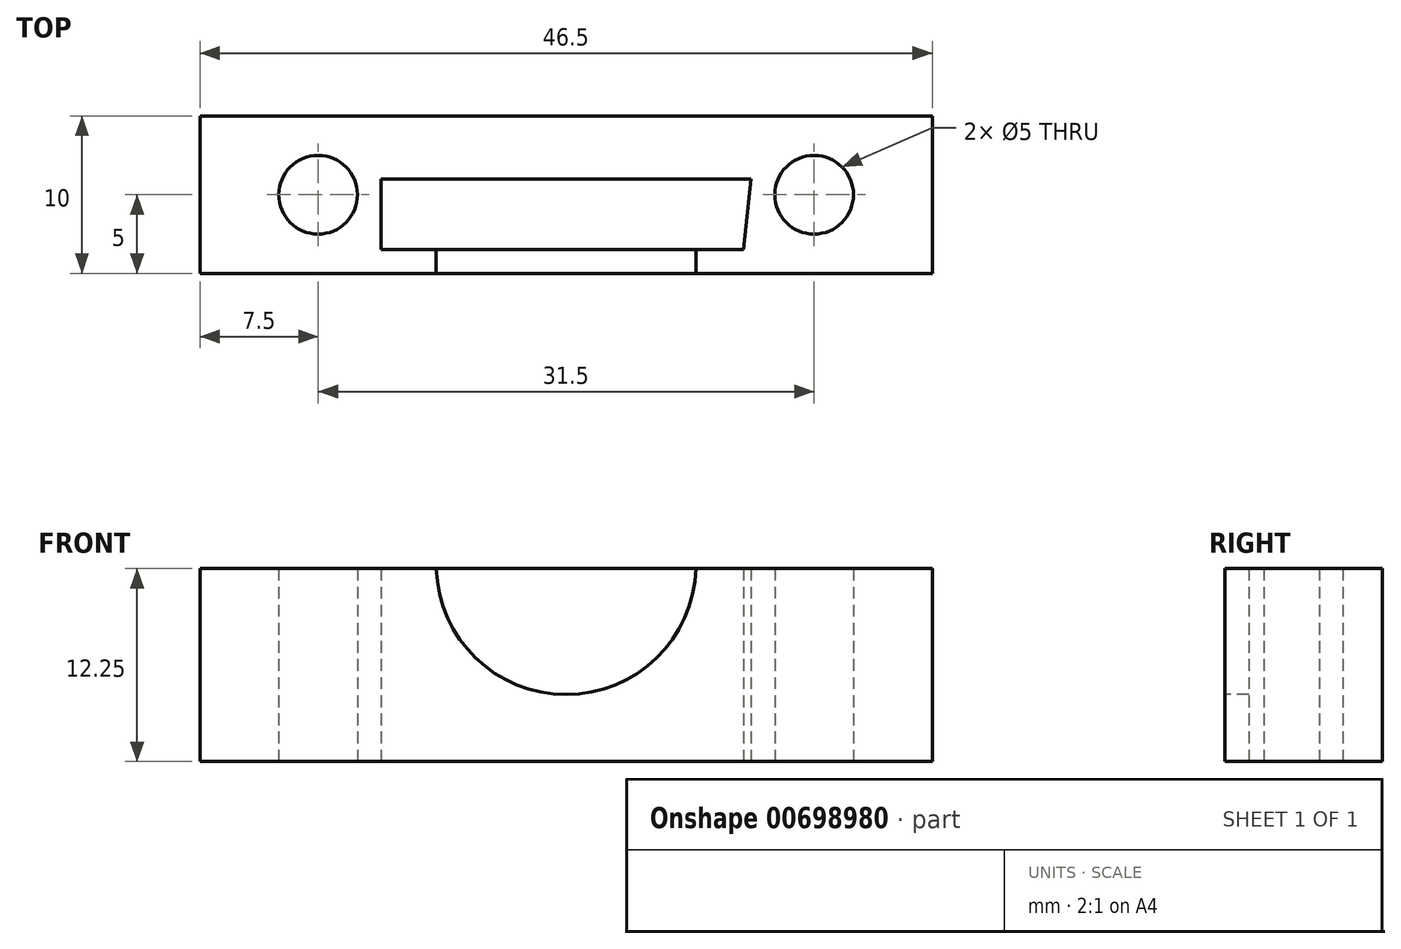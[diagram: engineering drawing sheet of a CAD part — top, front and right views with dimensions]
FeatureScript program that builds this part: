
annotation { "Feature Type Name" : "Feature", "Feature Type Description" : "" }
export const myFeature = defineFeature(function(context is Context, id is Id, definition is map)
    precondition{}
    {
        {
            var Q0;
            Q0=qCreatedBy(makeId("Top.planeOp"),FACE);
            var sketch = newSketch(context, id + "F0", { "sketchPlane" : qUnion([Q0])});
            skCircle(sketch, "E0", {"center": v(-15.75, 0) * mm, "radius": 2.5 * mm});
            skCircle(sketch, "E1", {"center": v(15.75, 0) * mm, "radius": 2.5 * mm});
            skLineSegment(sketch, "E2.bottom", {"start": v(-23.25, 5) * mm, "end": v(23.25, 5) * mm});
            skLineSegment(sketch, "E2.top", {"start": v(-23.25, -5) * mm, "end": v(23.25, -5) * mm});
            skLineSegment(sketch, "E2.left", {"start": v(-23.25, 5) * mm, "end": v(-23.25, -5) * mm});
            skLineSegment(sketch, "E2.right", {"start": v(23.25, 5) * mm, "end": v(23.25, -5) * mm});
            skLineSegment(sketch, "E3", {"start": v(-11.75, -3.47) * mm, "end": v(11.25, -3.47) * mm});
            skLineSegment(sketch, "E4.top", {"start": v(-11.75, 1) * mm, "end": v(11.75, 1) * mm});
            skLineSegment(sketch, "E5", {"start": v(-11.75, 1) * mm, "end": v(-11.75, -3.47) * mm});
            skLineSegment(sketch, "E6", {"start": v(11.75, 1) * mm, "end": v(11.25, -3.47) * mm});
            skSolve(sketch);
        }
        {
            var Q0;
            Q0=makeQuery(id+"F0.imprint","IMPRINT",FACE,{"disambiguationData":[TD([[makeQuery(id+"F0.imprint","IMPRINT",EDGE,{"derivedFrom":sQuery(id+"F0.wireOp",EDGE,"E0")}),-1.0]])]});
            extrude(context, id + "F1", {"entities" : qUnion([Q0]), "depth" : 12.25 * mm, "offsetDistance" : 25 * mm});
        }
        {
            var Q0;
            Q0=makeQuery(id+"F1.opExtrude","SWEPT_FACE",FACE,{"disambiguationData":[OSD([sQuery(id+"F0.wireOp",EDGE,"E2.top")])]});
            var sketch = newSketch(context, id + "F2", { "sketchPlane" : qUnion([Q0])});
            skCircle(sketch, "E7", {"center": v(0, 12.5) * mm, "radius": 8.25 * mm});
            skSolve(sketch);
        }
        {
            var Q0;
            Q0 = qSketchRegion(id + "F2", true);
            extrude(context, id + "F3", {"entities" : qUnion([Q0]), "operationType" : NewBodyOperationType.REMOVE, "oppositeDirection" : true, "depth" : 5 * mm, "offsetDistance" : 25 * mm});
        }
    });
